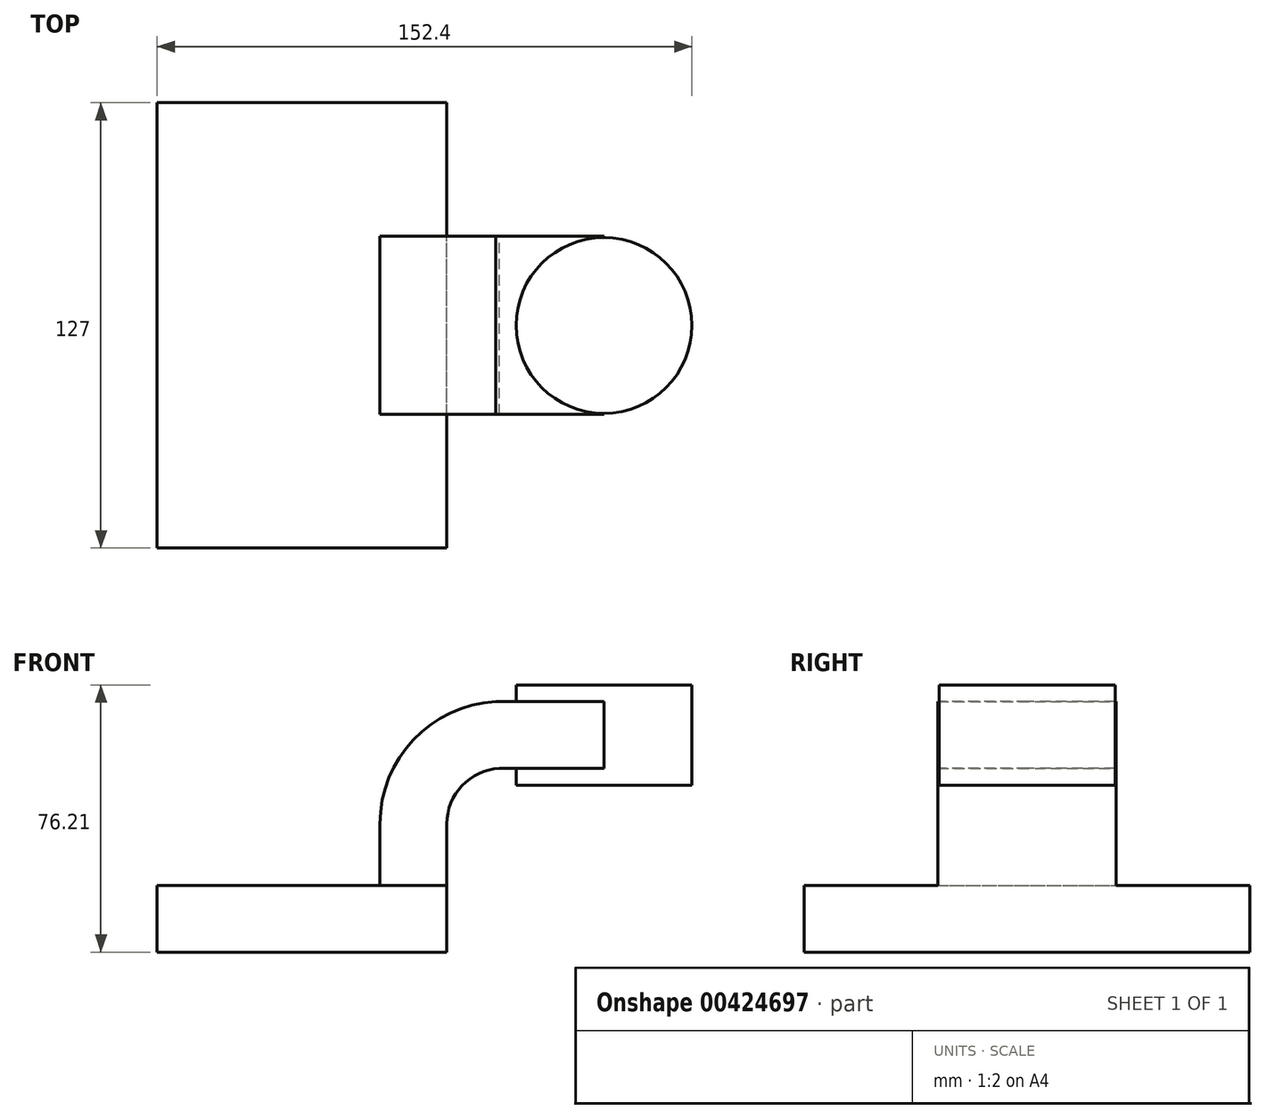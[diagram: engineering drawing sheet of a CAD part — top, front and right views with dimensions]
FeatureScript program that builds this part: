
annotation { "Feature Type Name" : "Feature", "Feature Type Description" : "" }
export const myFeature = defineFeature(function(context is Context, id is Id, definition is map)
    precondition{}
    {
        {
            var Q0;
            Q0=qCreatedBy(makeId("Front.planeOp"),FACE);
            var sketch = newSketch(context, id + "F0", { "sketchPlane" : qUnion([Q0])});
            skLineSegment(sketch, "E0.bottom", {"start": v(-41.28, 9.52) * mm, "end": v(41.27, 9.53) * mm});
            skLineSegment(sketch, "E0.top", {"start": v(-41.27, -9.53) * mm, "end": v(41.28, -9.53) * mm});
            skLineSegment(sketch, "E0.left", {"start": v(-41.28, 9.52) * mm, "end": v(-41.27, -9.53) * mm});
            skLineSegment(sketch, "E0.right", {"start": v(41.28, 9.53) * mm, "end": v(41.28, -9.52) * mm});
            skPoint(sketch, "E0.middle", {"position": v(0, 0) * mm});
            skLineSegment(sketch, "E1.bottom", {"start": v(111.13, 38.1) * mm, "end": v(60.33, 38.1) * mm});
            skLineSegment(sketch, "E1.top", {"start": v(111.13, 66.68) * mm, "end": v(60.32, 66.68) * mm});
            skLineSegment(sketch, "E1.left", {"start": v(111.12, 38.1) * mm, "end": v(111.12, 66.68) * mm});
            skLineSegment(sketch, "E1.right", {"start": v(60.33, 38.1) * mm, "end": v(60.33, 66.67) * mm});
            skPoint(sketch, "E1.middle", {"position": v(85.73, 52.39) * mm});
            skLineSegment(sketch, "E2", {"start": v(41.27, 9.53) * mm, "end": v(41.27, 27.02) * mm});
            skArc(sketch, "E3", {"start": v(41.28, 27.02) * mm, "mid": v(45.62, 37.93) * mm, "end": v(56.27, 42.88) * mm});
            skLineSegment(sketch, "E4", {"start": v(56.27, 42.88) * mm, "end": v(110.33, 42.88) * mm});
            skArc(sketch, "E5.0", {"start": v(22.23, 27.02) * mm, "mid": v(31.78, 51.03) * mm, "end": v(55.22, 61.9) * mm});
            skLineSegment(sketch, "E5.1", {"start": v(22.23, 9.53) * mm, "end": v(22.23, 27.02) * mm});
            skLineSegment(sketch, "E6", {"start": v(55.22, 61.9) * mm, "end": v(86.07, 61.9) * mm});
            skLineSegment(sketch, "E7", {"start": v(86.07, 38.1) * mm, "end": v(86.07, 66.68) * mm});
            skFitSpline(sketch, "E8", {"points": [v(-41.28, 9.52) * mm, v(55.22, 61.9) * mm], "startDerivative": vector(2.23, 59.34) * mm, "endDerivative": vector(88.95, 1.43) * mm});
            skSolve(sketch);
        }
        {
            var Q0;
            Q0=makeQuery(id+"F0.imprint","IMPRINT",FACE,{"disambiguationData":[TD([[makeQuery(id+"F0.imprint","IMPRINT",EDGE,{"derivedFrom":sQuery(id+"F0.wireOp",EDGE,"E0.top")}),1.0]])]});
            var Q1;
            Q1 = qSketchRegion(id + "FEC6onSmTzBPrEH_1", true);
            extrude(context, id + "F1", {"entities" : qUnion([Q0, Q1]), "endBound" : BoundingType.SYMMETRIC, "depth" : 127 * mm});
        }
        {
            var Q0;
            {var subQ1=sQuery(id+"F0.wireOp",EDGE,"E2");Q0=makeQuery(id+"F0.imprint","IMPRINT",FACE,{"disambiguationData":[TD([[makeQuery(id+"F0.imprint","IMPRINT",EDGE,{"derivedFrom":subQ1}),1.0]])]});}
            var Q1;
            {var subQ0=sQuery(id+"F0.wireOp",EDGE,"E4");var subQ1=sQuery(id+"F0.wireOp",EDGE,"E1.right");var subQ2=makeQuery(id+"F0.imprint","INTERSECT",VERTEX,{"derivedFrom":[subQ1,subQ0]});Q1=makeQuery(id+"F0.imprint","IMPRINT",FACE,{"disambiguationData":[TD([[makeQuery(id+"F0.imprint","IMPRINT",EDGE,{"disambiguationData":[TD([[subQ2,-1.0]])],"derivedFrom":subQ1}),-1.0]])]});}
            extrude(context, id + "F2", {"entities" : qUnion([Q0, Q1]), "operationType" : NewBodyOperationType.ADD, "endBound" : BoundingType.SYMMETRIC, "depth" : 50.8 * mm});
        }
        {
            var Q0;
            Q0=makeQuery(id+"F0.imprint","IMPRINT",FACE,{"disambiguationData":[TD([[makeQuery(id+"F0.imprint","IMPRINT",EDGE,{"derivedFrom":sQuery(id+"F0.wireOp",EDGE,"E5.0")}),1.0]])]});
            extrude(context, id + "F3", {"entities" : qUnion([Q0]), "operationType" : NewBodyOperationType.ADD, "endBound" : BoundingType.SYMMETRIC, "depth" : 15.88 * mm});
        }
        {
            var Q0;
            {var subQ4=sQuery(id+"F0.wireOp",EDGE,"E1.left");Q0=makeQuery(id+"F0.imprint","IMPRINT",FACE,{"disambiguationData":[TD([[makeQuery(id+"F0.imprint","IMPRINT",EDGE,{"derivedFrom":subQ4}),1.0]])]});}
            var Q1;
            Q1=sQuery(id+"F0.wireOp",EDGE,"E7");
            revolve(context, id + "F4", {"operationType" : NewBodyOperationType.ADD, "entities" : qUnion([Q0]), "axis" : qUnion([Q1]), "revolveType" : RevolveType.FULL});
        }
    });
